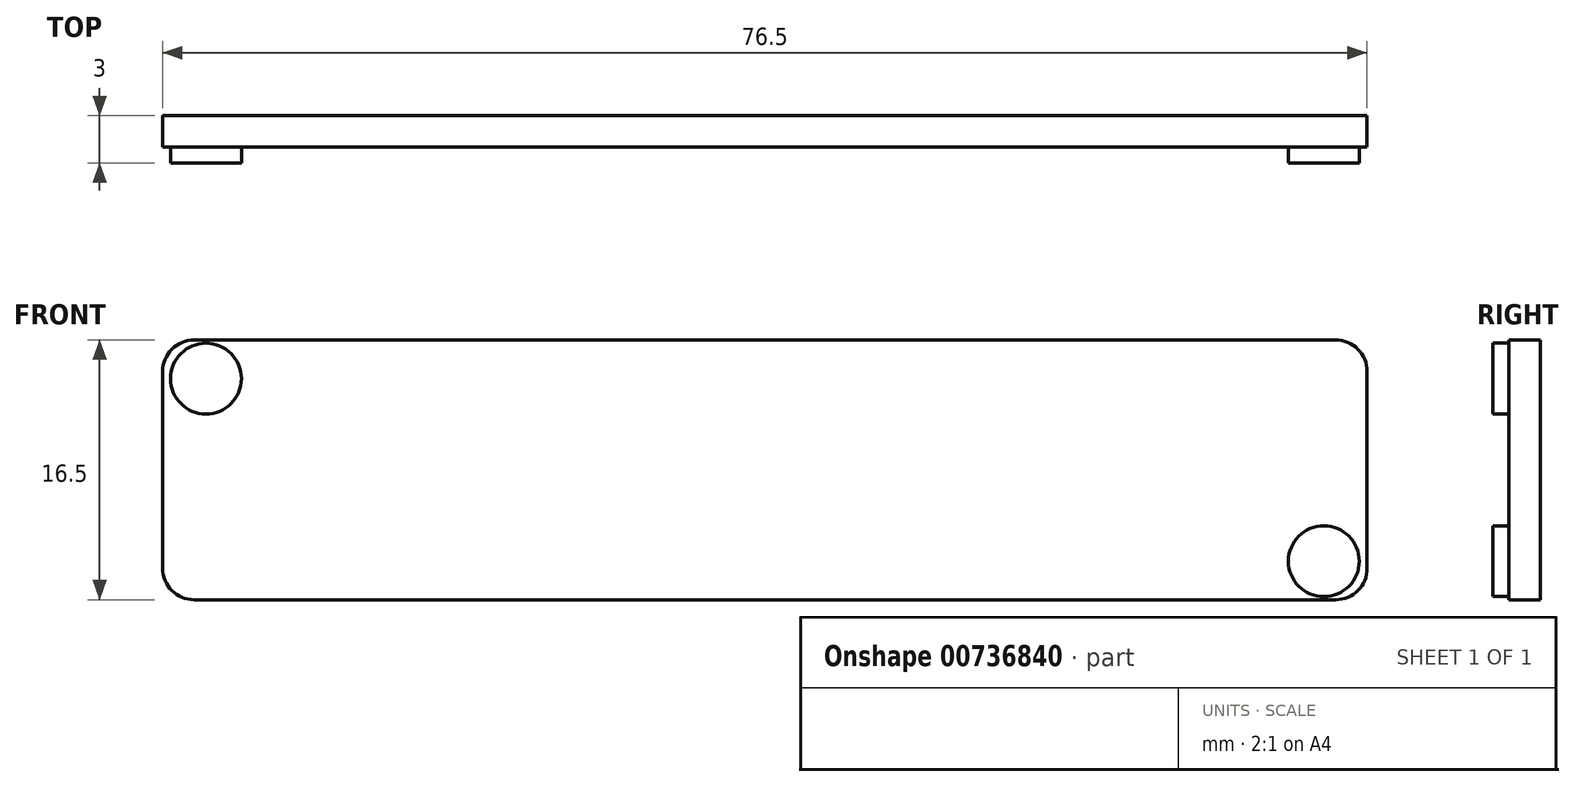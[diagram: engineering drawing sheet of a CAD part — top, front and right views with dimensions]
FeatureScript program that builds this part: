
annotation { "Feature Type Name" : "Feature", "Feature Type Description" : "" }
export const myFeature = defineFeature(function(context is Context, id is Id, definition is map)
    precondition{}
    {
        {
            var Q0;
            Q0=qCreatedBy(makeId("Front.planeOp"),FACE);
            var sketch = newSketch(context, id + "F0", { "sketchPlane" : qUnion([Q0])});
            skLineSegment(sketch, "E0.bottom", {"start": v(38.25, 8.25) * mm, "end": v(-38.25, 8.25) * mm});
            skLineSegment(sketch, "E0.top", {"start": v(38.25, -8.25) * mm, "end": v(-38.25, -8.25) * mm});
            skLineSegment(sketch, "E0.left", {"start": v(38.25, 8.25) * mm, "end": v(38.25, -8.25) * mm});
            skLineSegment(sketch, "E0.right", {"start": v(-38.25, 8.25) * mm, "end": v(-38.25, -8.25) * mm});
            skPoint(sketch, "E0.middle", {"position": v(0, 0) * mm});
            skSolve(sketch);
        }
        {
            var Q0;
            Q0=qCreatedBy(makeId("Front.planeOp"),FACE);
            var sketch = newSketch(context, id + "F1", { "sketchPlane" : qUnion([Q0])});
            skCircle(sketch, "E1", {"center": v(-35.5, 5.8) * mm, "radius": 2.25 * mm});
            skCircle(sketch, "E2", {"center": v(35.5, -5.8) * mm, "radius": 2.25 * mm});
            skSolve(sketch);
        }
        {
            var Q0;
            Q0=qSketchRegion(id+"F0",true);
            extrude(context, id + "F2", {"entities" : qUnion([Q0]), "oppositeDirection" : true, "depth" : 2 * mm, "offsetDistance" : 25 * mm});
        }
        {
            var Q0;
            Q0=qSketchRegion(id+"F1",true);
            extrude(context, id + "F3", {"entities" : qUnion([Q0]), "operationType" : NewBodyOperationType.ADD, "depth" : 1 * mm, "offsetDistance" : 25 * mm});
        }
        {
            var Q0;
            {var subQ0=sQuery(id+"F0.wireOp",EDGE,"E0.right");var subQ1=sQuery(id+"F0.wireOp",EDGE,"E0.bottom");Q0=makeQuery(id+"FJdqlX2h7RzJIyB_1.boolean.opBoolean","MERGE",EDGE,{"derivedFrom":[makeQuery(id+"F2.opExtrude","SWEPT_EDGE",EDGE,{"disambiguationData":[OSD([subQ1,subQ0])]}),makeQuery(id+"FJdqlX2h7RzJIyB_1.opExtrude","SWEPT_EDGE",EDGE,{"disambiguationData":[OSD([subQ1,subQ0])]})]});}
            var Q1;
            {var subQ0=sQuery(id+"F0.wireOp",EDGE,"E0.left");var subQ1=sQuery(id+"F0.wireOp",EDGE,"E0.bottom");Q1=makeQuery(id+"FJdqlX2h7RzJIyB_1.boolean.opBoolean","MERGE",EDGE,{"derivedFrom":[makeQuery(id+"F2.opExtrude","SWEPT_EDGE",EDGE,{"disambiguationData":[OSD([subQ1,subQ0])]}),makeQuery(id+"FJdqlX2h7RzJIyB_1.opExtrude","SWEPT_EDGE",EDGE,{"disambiguationData":[OSD([subQ1,subQ0])]})]});}
            var Q2;
            {var subQ0=sQuery(id+"F0.wireOp",EDGE,"E0.left");var subQ1=sQuery(id+"F0.wireOp",EDGE,"E0.top");Q2=makeQuery(id+"FJdqlX2h7RzJIyB_1.boolean.opBoolean","MERGE",EDGE,{"derivedFrom":[makeQuery(id+"F2.opExtrude","SWEPT_EDGE",EDGE,{"disambiguationData":[OSD([subQ1,subQ0])]}),makeQuery(id+"FJdqlX2h7RzJIyB_1.opExtrude","SWEPT_EDGE",EDGE,{"disambiguationData":[OSD([subQ1,subQ0])]})]});}
            var Q3;
            {var subQ0=sQuery(id+"F0.wireOp",EDGE,"E0.right");var subQ1=sQuery(id+"F0.wireOp",EDGE,"E0.top");Q3=makeQuery(id+"FJdqlX2h7RzJIyB_1.boolean.opBoolean","MERGE",EDGE,{"derivedFrom":[makeQuery(id+"F2.opExtrude","SWEPT_EDGE",EDGE,{"disambiguationData":[OSD([subQ1,subQ0])]}),makeQuery(id+"FJdqlX2h7RzJIyB_1.opExtrude","SWEPT_EDGE",EDGE,{"disambiguationData":[OSD([subQ1,subQ0])]})]});}
            fillet(context, id + "F4", {"entities" : qUnion([Q0, Q1, Q2, Q3]), "radius" : 2 * mm, "tangentPropagation" : true, "allowEdgeOverflow" : false});
        }
    });
